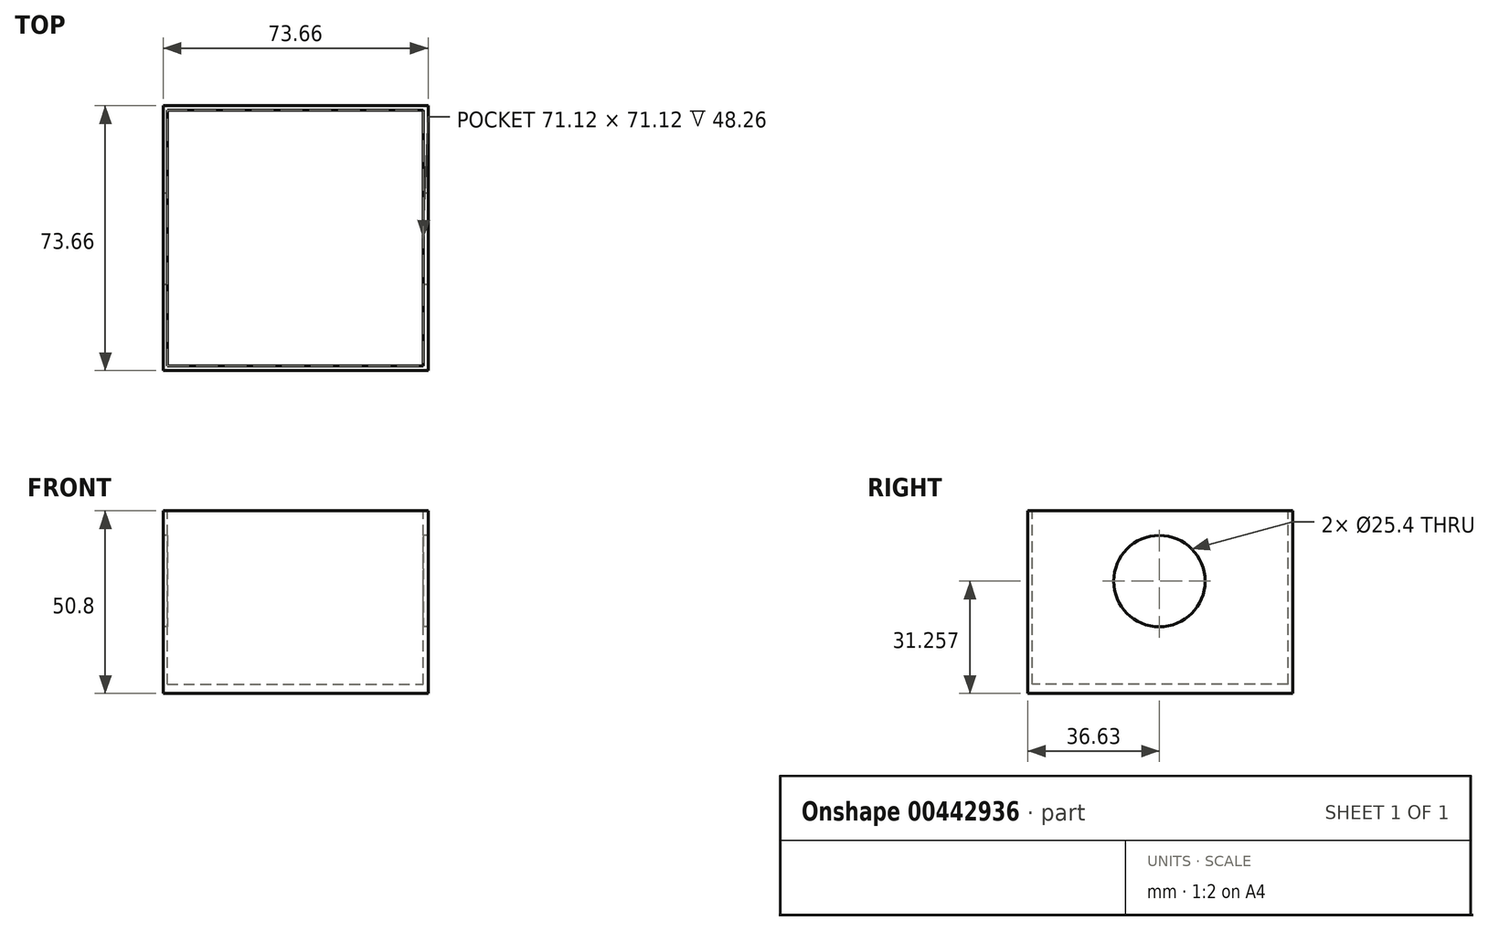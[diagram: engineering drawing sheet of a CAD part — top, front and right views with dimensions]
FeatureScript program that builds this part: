
annotation { "Feature Type Name" : "Feature", "Feature Type Description" : "" }
export const myFeature = defineFeature(function(context is Context, id is Id, definition is map)
    precondition{}
    {
        {
            var Q0;
            Q0=qCreatedBy(makeId("Top.planeOp"),FACE);
            var sketch = newSketch(context, id + "F0", { "sketchPlane" : qUnion([Q0])});
            skLineSegment(sketch, "E0.bottom", {"start": v(0, 61.13) * mm, "end": v(-73.66, 61.13) * mm});
            skLineSegment(sketch, "E0.top", {"start": v(0, -12.53) * mm, "end": v(-73.66, -12.53) * mm});
            skLineSegment(sketch, "E0.left", {"start": v(0, 61.13) * mm, "end": v(0, -12.53) * mm});
            skLineSegment(sketch, "E0.right", {"start": v(-73.66, 61.13) * mm, "end": v(-73.66, -12.53) * mm});
            skPoint(sketch, "E0.middle", {"position": v(-36.83, 24.3) * mm});
            skSolve(sketch);
        }
        {
            var Q0;
            Q0=makeQuery(id+"F0.imprint","IMPRINT",FACE,{"disambiguationData":[TD([[makeQuery(id+"F0.imprint","IMPRINT",EDGE,{"derivedFrom":sQuery(id+"F0.wireOp",EDGE,"E0.bottom")}),1.0]])]});
            extrude(context, id + "F1", {"entities" : qUnion([Q0]), "depth" : 50.8 * mm});
        }
        {
            var Q0;
            Q0=makeQuery(id+"F1.opExtrude","CAP_FACE",FACE,{"disambiguationData":[OSD([sQuery(id+"F0.wireOp",EDGE,"E0.bottom"),sQuery(id+"F0.wireOp",EDGE,"E0.top"),sQuery(id+"F0.wireOp",EDGE,"E0.left"),sQuery(id+"F0.wireOp",EDGE,"E0.right")])],"isStart":false});
            var sketch = newSketch(context, id + "F2", { "sketchPlane" : qUnion([Q0])});
            skLineSegment(sketch, "E1.bottom", {"start": v(-72.5, 59.91) * mm, "end": v(-1.37, 59.91) * mm});
            skLineSegment(sketch, "E1.top", {"start": v(-72.5, -11.2) * mm, "end": v(-1.37, -11.2) * mm});
            skLineSegment(sketch, "E1.left", {"start": v(-72.5, 59.91) * mm, "end": v(-72.5, -11.2) * mm});
            skLineSegment(sketch, "E1.right", {"start": v(-1.37, 59.91) * mm, "end": v(-1.37, -11.2) * mm});
            skPoint(sketch, "E1.middle", {"position": v(-36.93, 24.35) * mm});
            skSolve(sketch);
        }
        {
            var Q0;
            Q0=makeQuery(id+"F2.imprint","IMPRINT",FACE,{"disambiguationData":[TD([[makeQuery(id+"F2.imprint","IMPRINT",EDGE,{"derivedFrom":sQuery(id+"F2.wireOp",EDGE,"E1.bottom")}),-1.0]])]});
            extrude(context, id + "F3", {"entities" : qUnion([Q0]), "operationType" : NewBodyOperationType.REMOVE, "oppositeDirection" : true, "depth" : 48.26 * mm});
        }
        {
            var Q0;
            Q0=makeQuery(id+"F1.opExtrude","SWEPT_FACE",FACE,{"disambiguationData":[OSD([sQuery(id+"F0.wireOp",EDGE,"E0.right")])]});
            var sketch = newSketch(context, id + "F4", { "sketchPlane" : qUnion([Q0])});
            skCircle(sketch, "E2", {"center": v(-24.1, 31.26) * mm, "radius": 12.7 * mm});
            skSolve(sketch);
        }
        {
            var Q0;
            Q0=makeQuery(id+"F4.imprint","IMPRINT",FACE,{"disambiguationData":[TD([[makeQuery(id+"F4.imprint","IMPRINT",EDGE,{"derivedFrom":sQuery(id+"F4.wireOp",EDGE,"E2")}),1.0]])]});
            extrude(context, id + "F5", {"entities" : qUnion([Q0]), "operationType" : NewBodyOperationType.REMOVE, "oppositeDirection" : true, "depth" : 87.38 * mm});
        }
    });
